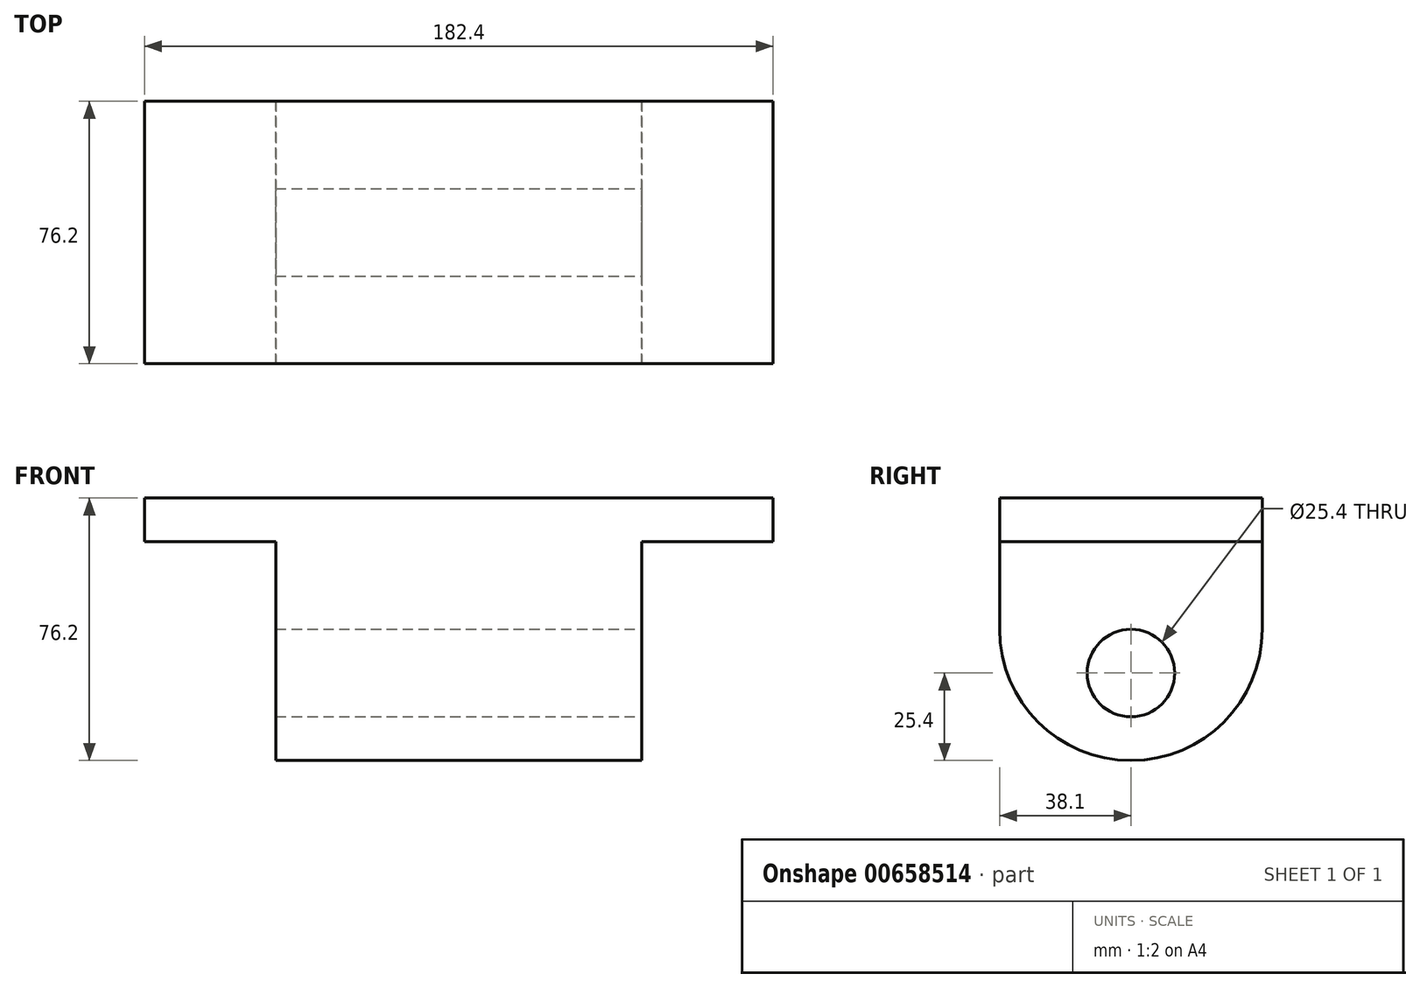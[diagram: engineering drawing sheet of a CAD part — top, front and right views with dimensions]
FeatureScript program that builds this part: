
annotation { "Feature Type Name" : "Feature", "Feature Type Description" : "" }
export const myFeature = defineFeature(function(context is Context, id is Id, definition is map)
    precondition{}
    {
        {
            var Q0;
            Q0=qCreatedBy(makeId("Top.planeOp"),FACE);
            var sketch = newSketch(context, id + "F0", { "sketchPlane" : qUnion([Q0])});
            skLineSegment(sketch, "E0.bottom", {"start": v(0, 0) * mm, "end": v(182.4, 0) * mm});
            skLineSegment(sketch, "E0.top", {"start": v(0, 76.2) * mm, "end": v(182.4, 76.2) * mm});
            skLineSegment(sketch, "E0.left", {"start": v(0, 0) * mm, "end": v(0, 76.2) * mm});
            skLineSegment(sketch, "E0.right", {"start": v(182.4, 0) * mm, "end": v(182.4, 76.2) * mm});
            skSolve(sketch);
        }
        {
            var Q0;
            Q0=makeQuery(id+"F0.imprint","IMPRINT",FACE,{"disambiguationData":[TD([[makeQuery(id+"F0.imprint","IMPRINT",EDGE,{"derivedFrom":sQuery(id+"F0.wireOp",EDGE,"E0.bottom")}),1.0]])]});
            extrude(context, id + "F1", {"entities" : qUnion([Q0]), "depth" : 76.2 * mm, "offsetDistance" : 25.4 * mm});
        }
        {
            var Q0;
            Q0=makeQuery(id+"F1.opExtrude","CAP_FACE",FACE,{"disambiguationData":[OSD([sQuery(id+"F0.wireOp",EDGE,"E0.bottom"),sQuery(id+"F0.wireOp",EDGE,"E0.top"),sQuery(id+"F0.wireOp",EDGE,"E0.left"),sQuery(id+"F0.wireOp",EDGE,"E0.right")])],"isStart":true});
            var sketch = newSketch(context, id + "F2", { "sketchPlane" : qUnion([Q0])});
            skLineSegment(sketch, "E1.bottom", {"start": v(182.4, -76.2) * mm, "end": v(144.3, -76.2) * mm});
            skLineSegment(sketch, "E1.top", {"start": v(182.4, 0) * mm, "end": v(144.3, 0) * mm});
            skLineSegment(sketch, "E1.left", {"start": v(182.4, -76.2) * mm, "end": v(182.4, 0) * mm});
            skLineSegment(sketch, "E1.right", {"start": v(144.3, -76.2) * mm, "end": v(144.3, 0) * mm});
            skLineSegment(sketch, "E2.bottom", {"start": v(0, 0) * mm, "end": v(38.1, 0) * mm});
            skLineSegment(sketch, "E2.top", {"start": v(0, -76.2) * mm, "end": v(38.1, -76.2) * mm});
            skLineSegment(sketch, "E2.left", {"start": v(0, 0) * mm, "end": v(0, -76.2) * mm});
            skLineSegment(sketch, "E2.right", {"start": v(38.1, 0) * mm, "end": v(38.1, -76.2) * mm});
            skSolve(sketch);
        }
        {
            var Q0;
            Q0=makeQuery(id+"F2.imprint","IMPRINT",FACE,{"disambiguationData":[TD([[makeQuery(id+"F2.imprint","IMPRINT",EDGE,{"derivedFrom":sQuery(id+"F2.wireOp",EDGE,"E1.bottom")}),1.0]])]});
            var Q1;
            Q1=makeQuery(id+"F2.imprint","IMPRINT",FACE,{"disambiguationData":[TD([[makeQuery(id+"F2.imprint","IMPRINT",EDGE,{"derivedFrom":sQuery(id+"F2.wireOp",EDGE,"E2.bottom")}),-1.0]])]});
            extrude(context, id + "F3", {"entities" : qUnion([Q0, Q1]), "operationType" : NewBodyOperationType.REMOVE, "oppositeDirection" : true, "depth" : 63.5 * mm, "offsetDistance" : 25.4 * mm});
        }
        {
            var Q0;
            Q0=makeQuery(id+"F1.opExtrude","CAP_EDGE",EDGE,{"disambiguationData":[OSD([sQuery(id+"F0.wireOp",EDGE,"E0.bottom")])],"isStart":true});
            var Q1;
            Q1=makeQuery(id+"F1.opExtrude","CAP_EDGE",EDGE,{"disambiguationData":[OSD([sQuery(id+"F0.wireOp",EDGE,"E0.top")])],"isStart":true});
            fillet(context, id + "F4", {"entities" : qUnion([Q0, Q1]), "radius" : 38.1 * mm, "tangentPropagation" : true, "allowEdgeOverflow" : false});
        }
        {
            var Q0;
            Q0=makeQuery(id+"F3.boolean.opBoolean","COPY",FACE,{"derivedFrom":makeQuery(id+"F3.opExtrude","SWEPT_FACE",FACE,{"disambiguationData":[OSD([sQuery(id+"F2.wireOp",EDGE,"E1.right")])]})});
            var sketch = newSketch(context, id + "F5", { "sketchPlane" : qUnion([Q0])});
            skCircle(sketch, "E3", {"center": v(38.1, 25.4) * mm, "radius": 12.7 * mm});
            skSolve(sketch);
        }
        {
            var Q0;
            Q0=makeQuery(id+"F5.imprint","IMPRINT",FACE,{"disambiguationData":[TD([[makeQuery(id+"F5.imprint","IMPRINT",EDGE,{"derivedFrom":sQuery(id+"F5.wireOp",EDGE,"E3")}),1.0]])]});
            extrude(context, id + "F6", {"entities" : qUnion([Q0]), "operationType" : NewBodyOperationType.REMOVE, "endBound" : BoundingType.THROUGH_ALL, "oppositeDirection" : true, "depth" : 25.4 * mm, "offsetDistance" : 25.4 * mm});
        }
    });
